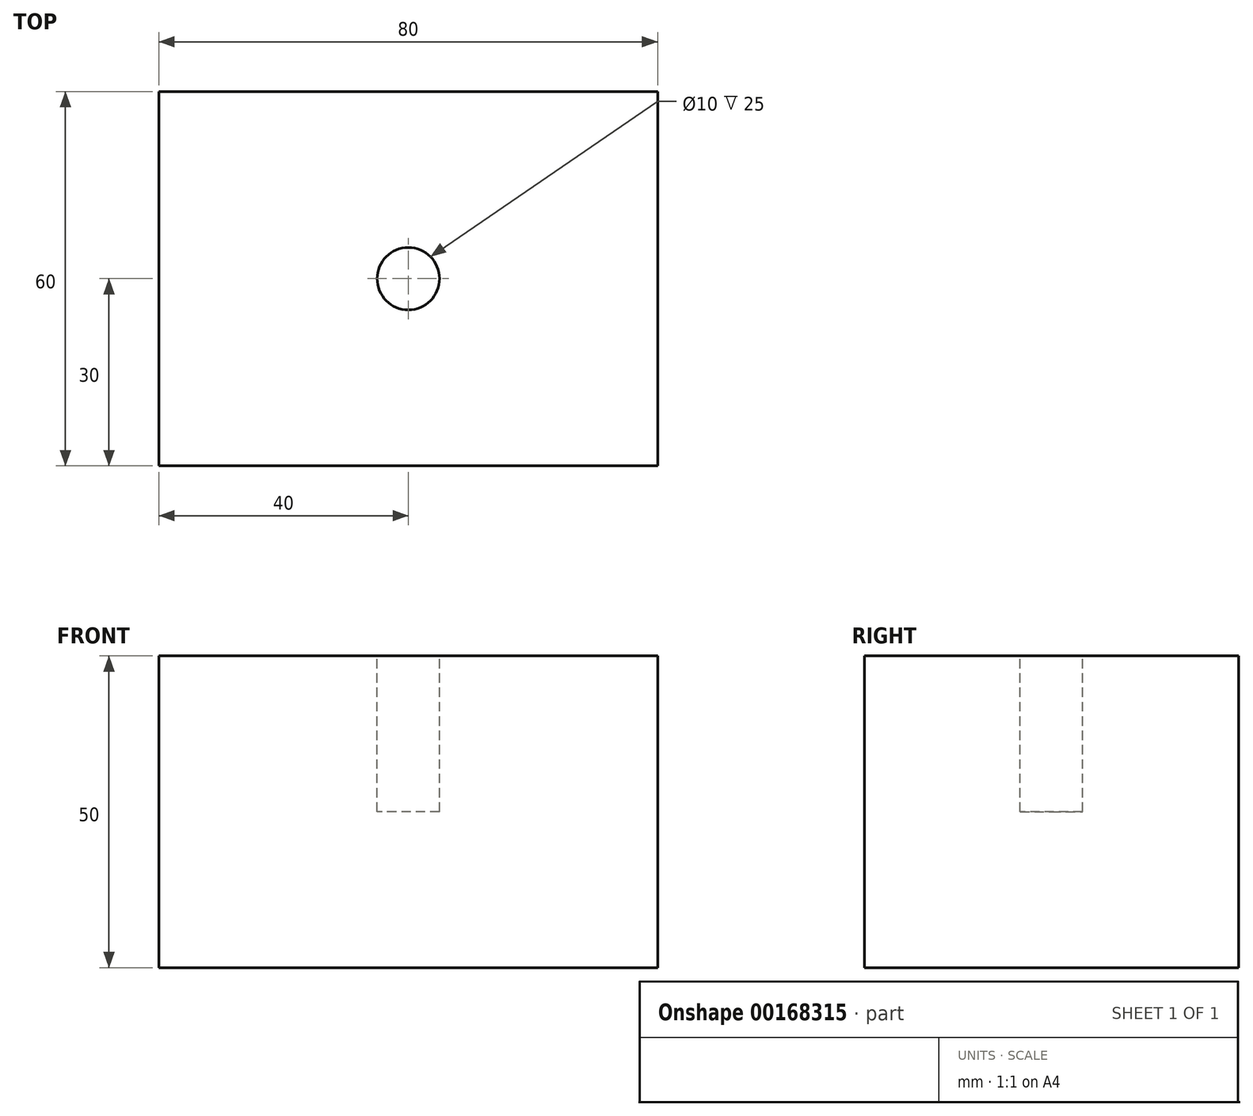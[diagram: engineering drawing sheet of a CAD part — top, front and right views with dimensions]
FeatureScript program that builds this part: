
annotation { "Feature Type Name" : "Feature", "Feature Type Description" : "" }
export const myFeature = defineFeature(function(context is Context, id is Id, definition is map)
    precondition{}
    {
        {
            var Q0;
            Q0=qCreatedBy(makeId("Top.planeOp"),FACE);
            var sketch = newSketch(context, id + "F0", { "sketchPlane" : qUnion([Q0])});
            skLineSegment(sketch, "E0.bottom", {"start": v(40, 30) * mm, "end": v(-40, 30) * mm});
            skLineSegment(sketch, "E0.top", {"start": v(40, -30) * mm, "end": v(-40, -30) * mm});
            skLineSegment(sketch, "E0.left", {"start": v(40, 30) * mm, "end": v(40, -30) * mm});
            skLineSegment(sketch, "E0.right", {"start": v(-40, 30) * mm, "end": v(-40, -30) * mm});
            skPoint(sketch, "E0.middle", {"position": v(0, 0) * mm});
            skSolve(sketch);
        }
        {
            var Q0;
            Q0 = qSketchRegion(id + "FCzHVEe2VD0Qz9i_0", true);
            var Q1;
            Q1=makeQuery(id+"F0.imprint","IMPRINT",FACE,{"disambiguationData":[TD([[makeQuery(id+"F0.imprint","IMPRINT",EDGE,{"derivedFrom":sQuery(id+"F0.wireOp",EDGE,"E0.bottom")}),1.0]])]});
            var Q2;
            Q2=makeQuery(id+"FCzHVEe2VD0Qz9i_0.imprint","IMPRINT",FACE,{"disambiguationData":[TD([[makeQuery(id+"FCzHVEe2VD0Qz9i_0.imprint","IMPRINT",EDGE,{"derivedFrom":makeQuery(id+"F0.imprint","IMPRINT",EDGE,{"derivedFrom":sQuery(id+"F0.wireOp",EDGE,"E0.bottom")})}),1.0]])]});
            extrude(context, id + "F1", {"entities" : qUnion([Q0, Q1, Q2]), "depth" : 50 * mm});
        }
        {
            var Q0;
            {var subQ0=sQuery(id+"F0.wireOp",EDGE,"E0.right");var subQ1=sQuery(id+"F0.wireOp",EDGE,"E0.left");var subQ2=sQuery(id+"F0.wireOp",EDGE,"E0.top");var subQ3=sQuery(id+"F0.wireOp",EDGE,"E0.bottom");Q0=makeQuery(id+"F1.opExtrude","CAP_FACE",FACE,{"disambiguationData":[OSD([subQ3,subQ2,subQ1,subQ0]),TDD([makeQuery(id+"F0.imprint","IMPRINT",EDGE,{"derivedFrom":subQ3}),makeQuery(id+"F0.imprint","IMPRINT",EDGE,{"derivedFrom":subQ2}),makeQuery(id+"F0.imprint","IMPRINT",EDGE,{"derivedFrom":subQ1}),makeQuery(id+"F0.imprint","IMPRINT",EDGE,{"derivedFrom":subQ0})])],"isStart":false});}
            var sketch = newSketch(context, id + "F2", { "sketchPlane" : qUnion([Q0])});
            skCircle(sketch, "E1", {"center": v(0, 0) * mm, "radius": 5 * mm});
            skSolve(sketch);
        }
        {
            var Q0;
            Q0 = qSketchRegion(id + "F2", true);
            extrude(context, id + "F3", {"entities" : qUnion([Q0]), "operationType" : NewBodyOperationType.REMOVE, "oppositeDirection" : true, "depth" : 25 * mm});
        }
    });
